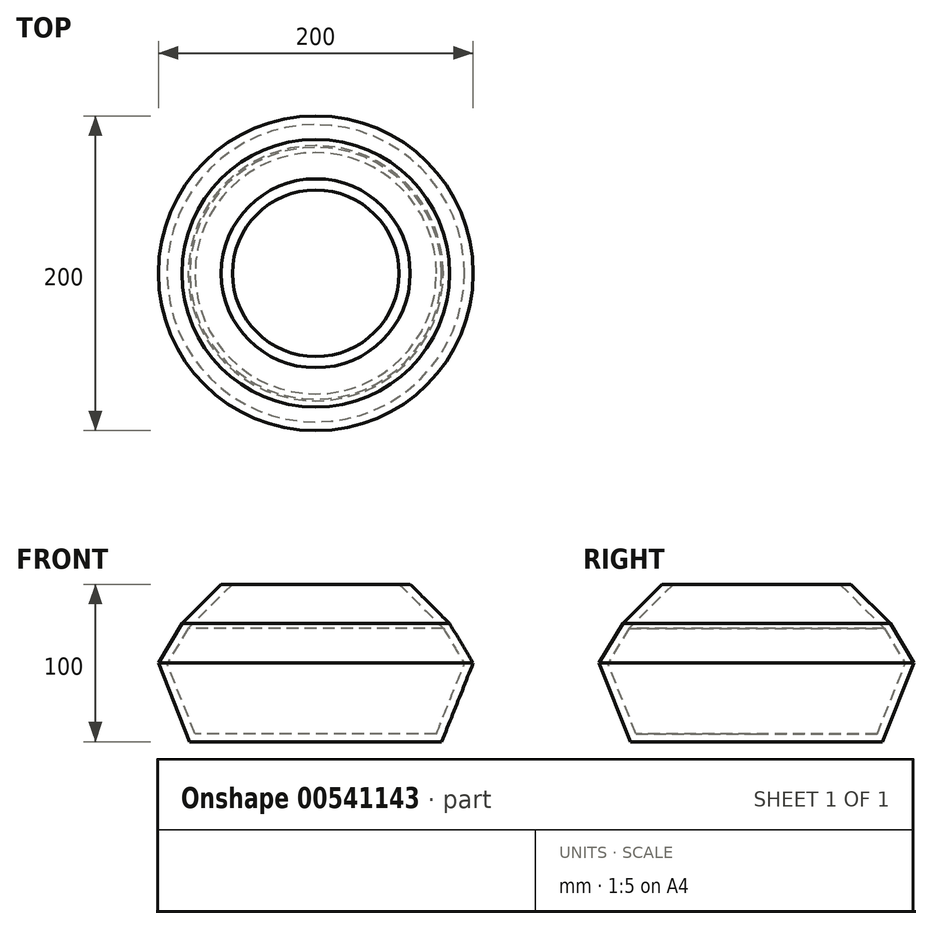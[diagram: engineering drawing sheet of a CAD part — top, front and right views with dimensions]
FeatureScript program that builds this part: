
annotation { "Feature Type Name" : "Feature", "Feature Type Description" : "" }
export const myFeature = defineFeature(function(context is Context, id is Id, definition is map)
    precondition{}
    {
        {
            var Q0;
            Q0=qCreatedBy(makeId("Top.planeOp"),FACE);
            var sketch = newSketch(context, id + "F0", { "sketchPlane" : qUnion([Q0])});
            skCircle(sketch, "E0", {"center": v(0, 0) * mm, "radius": 80 * mm});
            skSolve(sketch);
        }
        {
            var Q0;
            Q0=qCreatedBy(makeId("Top.planeOp"),FACE);
            cPlane(context, id + "F1", {"entities" : qUnion([Q0]), "cplaneType" : CPlaneType.OFFSET, "offset" : 25 * mm, "width" : 150 * mm, "height" : 150 * mm});
        }
        {
            var Q0;
            Q0=qCreatedBy(id+"F1.planeOp",FACE);
            var sketch = newSketch(context, id + "F2", { "sketchPlane" : qUnion([Q0])});
            skCircle(sketch, "E1", {"center": v(0, 0) * mm, "radius": 90 * mm});
            skSolve(sketch);
        }
        {
            var Q0;
            Q0 = qSketchRegion(id + "F0", true);
            var Q1;
            Q1 = qSketchRegion(id + "F2", true);
            loft(context, id + "F3", {"sheetProfilesArray" : [{ "sheetProfileEntities" : qUnion([Q0]) }, { "sheetProfileEntities" : qUnion([Q1]) }]});
        }
        {
            var Q0;
            Q0=qCreatedBy(id+"F1.planeOp",FACE);
            cPlane(context, id + "F4", {"entities" : qUnion([Q0]), "cplaneType" : CPlaneType.OFFSET, "offset" : 25 * mm, "width" : 150 * mm, "height" : 150 * mm});
        }
        {
            var Q0;
            Q0=qCreatedBy(id+"F4.planeOp",FACE);
            var sketch = newSketch(context, id + "F5", { "sketchPlane" : qUnion([Q0])});
            skCircle(sketch, "E2", {"center": v(0, 0) * mm, "radius": 100 * mm});
            skSolve(sketch);
        }
        {
            var Q1;
            Q1=makeQuery(id+"F3.opLoft","CAP_FACE",FACE,{"disambiguationData":[OSD([makeQuery(id+"F2.imprint","IMPRINT",FACE,{"disambiguationData":[TD([[makeQuery(id+"F2.imprint","IMPRINT",EDGE,{"derivedFrom":sQuery(id+"F2.wireOp",EDGE,"E1")}),1.0]])]})])],"isStart":true});
            var Q2;
            Q2 = qSketchRegion(id + "F5", true);
            loft(context, id + "F6", {"operationType" : NewBodyOperationType.ADD, "sheetProfilesArray" : [{ "sheetProfileEntities" : qUnion([Q1]) }, { "sheetProfileEntities" : qUnion([Q2]) }]});
        }
        {
            var Q0;
            Q0=qCreatedBy(id+"F4.planeOp",FACE);
            cPlane(context, id + "F7", {"entities" : qUnion([Q0]), "cplaneType" : CPlaneType.OFFSET, "offset" : 25 * mm, "width" : 150 * mm, "height" : 150 * mm});
        }
        {
            var Q0;
            Q0=qCreatedBy(id+"F7.planeOp",FACE);
            var sketch = newSketch(context, id + "F8", { "sketchPlane" : qUnion([Q0])});
            skCircle(sketch, "E3", {"center": v(0, 0) * mm, "radius": 85 * mm});
            skSolve(sketch);
        }
        {
            var Q1;
            Q1=makeQuery(id+"F6.opLoft","CAP_FACE",FACE,{"disambiguationData":[OSD([makeQuery(id+"F5.imprint","IMPRINT",FACE,{"disambiguationData":[TD([[makeQuery(id+"F5.imprint","IMPRINT",EDGE,{"derivedFrom":sQuery(id+"F5.wireOp",EDGE,"E2")}),1.0]])]})])],"isStart":true});
            var Q2;
            Q2 = qSketchRegion(id + "F8", true);
            loft(context, id + "F9", {"operationType" : NewBodyOperationType.ADD, "sheetProfilesArray" : [{ "sheetProfileEntities" : qUnion([Q1]) }, { "sheetProfileEntities" : qUnion([Q2]) }]});
        }
        {
            var Q0;
            Q0=qCreatedBy(id+"F7.planeOp",FACE);
            cPlane(context, id + "F10", {"entities" : qUnion([Q0]), "cplaneType" : CPlaneType.OFFSET, "offset" : 25 * mm, "width" : 150 * mm, "height" : 150 * mm});
        }
        {
            var Q0;
            Q0=qCreatedBy(id+"F10.planeOp",FACE);
            var sketch = newSketch(context, id + "F11", { "sketchPlane" : qUnion([Q0])});
            skCircle(sketch, "E4", {"center": v(0, 0) * mm, "radius": 60 * mm});
            skSolve(sketch);
        }
        {
            var Q1;
            Q1=makeQuery(id+"F9.opLoft","CAP_FACE",FACE,{"disambiguationData":[OSD([makeQuery(id+"F8.imprint","IMPRINT",FACE,{"disambiguationData":[TD([[makeQuery(id+"F8.imprint","IMPRINT",EDGE,{"derivedFrom":sQuery(id+"F8.wireOp",EDGE,"E3")}),1.0]])]})])],"isStart":true});
            var Q2;
            Q2 = qSketchRegion(id + "F11", true);
            loft(context, id + "F12", {"operationType" : NewBodyOperationType.ADD, "sheetProfilesArray" : [{ "sheetProfileEntities" : qUnion([Q1]) }, { "sheetProfileEntities" : qUnion([Q2]) }]});
        }
        {
            var Q0;
            Q0=makeQuery(id+"F12.opLoft","CAP_FACE",FACE,{"disambiguationData":[OSD([makeQuery(id+"F11.imprint","IMPRINT",FACE,{"disambiguationData":[TD([[makeQuery(id+"F11.imprint","IMPRINT",EDGE,{"derivedFrom":sQuery(id+"F11.wireOp",EDGE,"E4")}),1.0]])]})])],"isStart":true});
            shell(context, id + "F13", {"entities" : qUnion([Q0]), "thickness" : 5 * mm});
        }
    });
